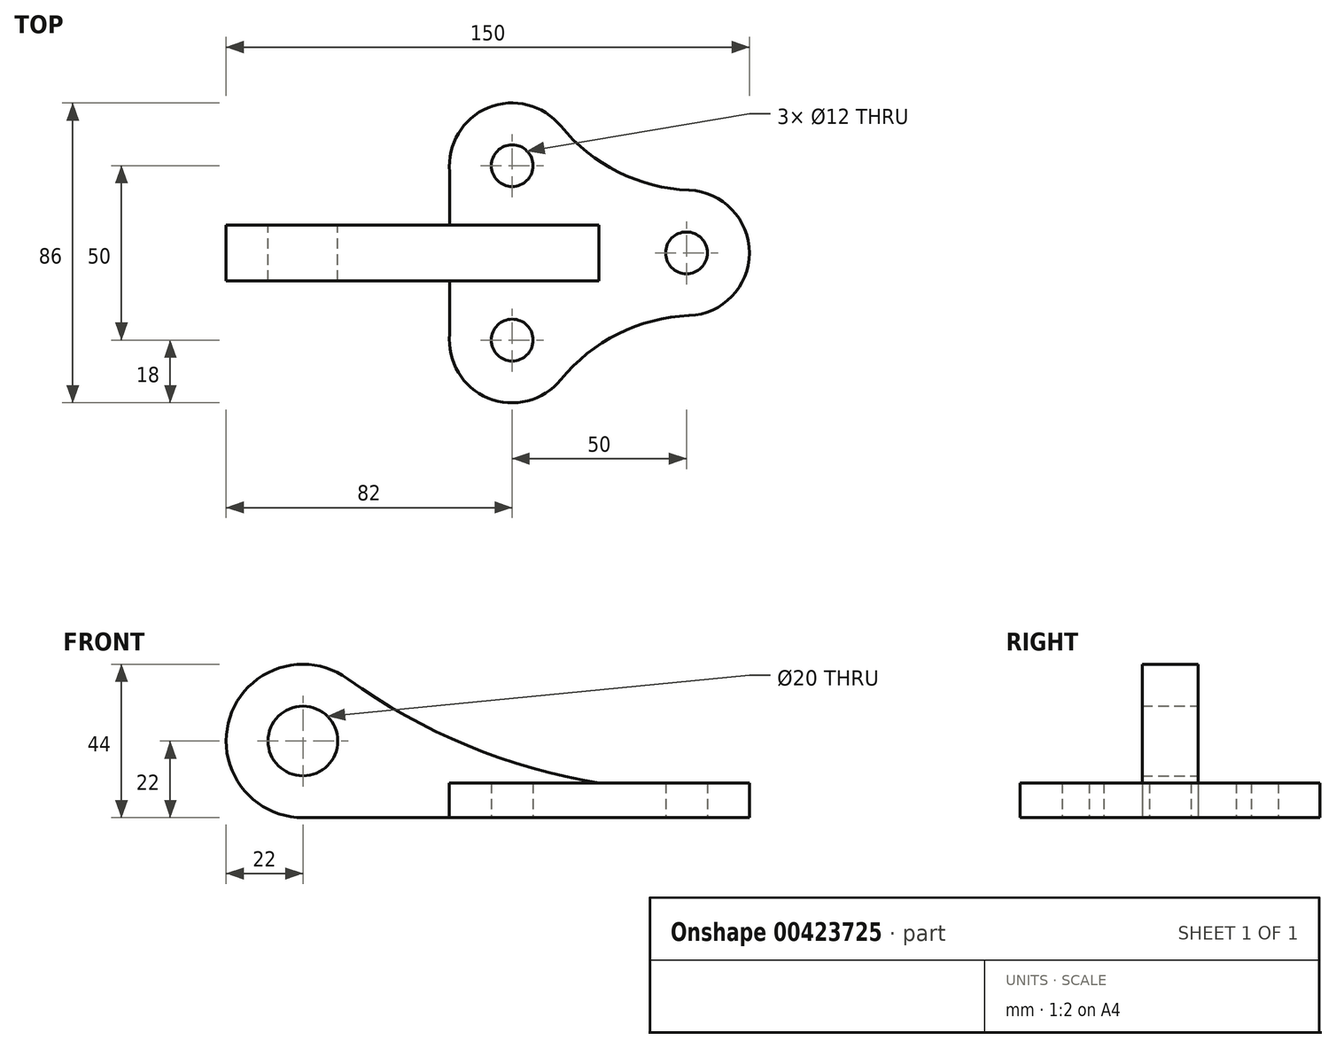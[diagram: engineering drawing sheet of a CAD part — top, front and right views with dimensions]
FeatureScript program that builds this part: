
annotation { "Feature Type Name" : "Feature", "Feature Type Description" : "" }
export const myFeature = defineFeature(function(context is Context, id is Id, definition is map)
    precondition{}
    {
        {
            var Q0;
            Q0=qCreatedBy(makeId("Top.planeOp"),FACE);
            var sketch = newSketch(context, id + "F0", { "sketchPlane" : qUnion([Q0])});
            skPoint(sketch, "E0.endSnap0", {"position": v(0, 12.5) * mm});
            skCircle(sketch, "E1", {"center": v(0, 25) * mm, "radius": 6 * mm});
            skCircle(sketch, "E2", {"center": v(0, -25) * mm, "radius": 6 * mm});
            skCircle(sketch, "E3", {"center": v(50, 0) * mm, "radius": 6 * mm});
            skArc(sketch, "E4", {"start": v(13.96, 36.37) * mm, "mid": v(-6.86, 41.64) * mm, "end": v(-17.91, 23.23) * mm});
            skArc(sketch, "E5", {"start": v(-17.91, -23.23) * mm, "mid": v(-6.86, -41.64) * mm, "end": v(13.96, -36.37) * mm});
            skArc(sketch, "E6", {"start": v(50.72, -17.99) * mm, "mid": v(68, 0) * mm, "end": v(50.72, 17.99) * mm});
            skArc(sketch, "E7", {"start": v(50.72, -17.99) * mm, "mid": v(30.36, -23.22) * mm, "end": v(13.96, -36.37) * mm});
            skArc(sketch, "E8", {"start": v(13.96, 36.37) * mm, "mid": v(30.36, 23.22) * mm, "end": v(50.72, 17.99) * mm});
            skLineSegment(sketch, "E9", {"start": v(-17.91, 23.23) * mm, "end": v(-17.91, -23.23) * mm});
            skSolve(sketch);
        }
        {
            var Q0;
            Q0=makeQuery(id+"F0.imprint","IMPRINT",FACE,{"disambiguationData":[TD([[makeQuery(id+"F0.imprint","IMPRINT",EDGE,{"derivedFrom":sQuery(id+"F0.wireOp",EDGE,"E1")}),-1.0]])]});
            extrude(context, id + "F1", {"entities" : qUnion([Q0]), "depth" : 10 * mm});
        }
        {
            var Q0;
            Q0=qCreatedBy(makeId("Front.planeOp"),FACE);
            var sketch = newSketch(context, id + "F2", { "sketchPlane" : qUnion([Q0])});
            skArc(sketch, "E10", {"start": v(-47.13, 39.84) * mm, "mid": v(-80.93, 28.76) * mm, "end": v(-60, 0) * mm});
            skPoint(sketch, "E11.startSnap0", {"position": v(50, 10) * mm});
            skLineSegment(sketch, "E12.0.0", {"start": v(13.96, 0) * mm, "end": v(50.72, 0) * mm, "construction": true});
            skLineSegment(sketch, "E12.0.1", {"start": v(50.72, 0) * mm, "end": v(50.72, 10) * mm, "construction": true});
            skLineSegment(sketch, "E12.0.3", {"start": v(13.96, 10) * mm, "end": v(13.96, 0) * mm, "construction": true});
            skCircle(sketch, "E13", {"center": v(-60, 22) * mm, "radius": 10 * mm});
            skArc(sketch, "E14", {"start": v(-47.13, 39.84) * mm, "mid": v(-12.84, 20.71) * mm, "end": v(24.94, 10) * mm});
            skLineSegment(sketch, "E15", {"start": v(24.94, 10) * mm, "end": v(24.94, 0) * mm});
            skLineSegment(sketch, "E16", {"start": v(-60, 0) * mm, "end": v(24.94, 0) * mm});
            skSolve(sketch);
        }
        {
            var Q0;
            Q0 = qSketchRegion(id + "F2", true);
            extrude(context, id + "F3", {"entities" : qUnion([Q0]), "operationType" : NewBodyOperationType.ADD, "depth" : 8 * mm, "hasSecondDirection" : true, "secondDirectionOppositeDirection" : true, "secondDirectionDepth" : 8 * mm});
        }
    });
